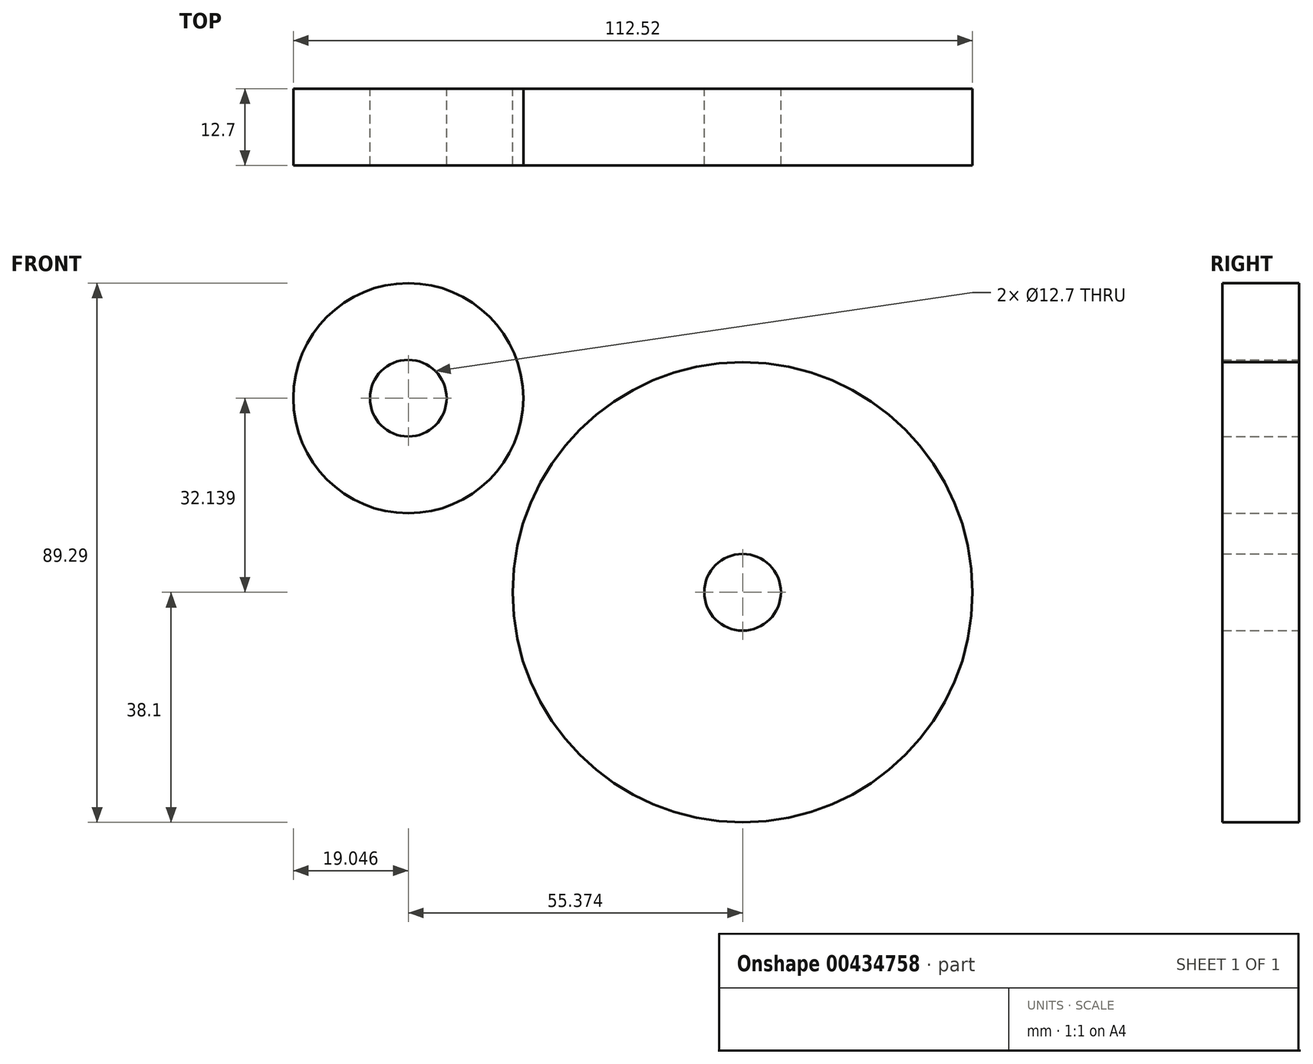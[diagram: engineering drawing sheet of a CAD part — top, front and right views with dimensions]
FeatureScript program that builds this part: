
annotation { "Feature Type Name" : "Feature", "Feature Type Description" : "" }
export const myFeature = defineFeature(function(context is Context, id is Id, definition is map)
    precondition{}
    {
        {
            var Q0;
            Q0=qCreatedBy(makeId("Front.planeOp"),FACE);
            var sketch = newSketch(context, id + "F0", { "sketchPlane" : qUnion([Q0])});
            skCircle(sketch, "E0", {"center": v(0, 0) * mm, "radius": 38.1 * mm});
            skCircle(sketch, "E1", {"center": v(0, 0) * mm, "radius": 6.35 * mm});
            skCircle(sketch, "E2", {"center": v(-55.37, 32.14) * mm, "radius": 19.05 * mm});
            skCircle(sketch, "E3", {"center": v(-55.37, 32.14) * mm, "radius": 6.35 * mm});
            skSolve(sketch);
        }
        {
            var Q0;
            Q0=makeQuery(id+"F0.imprint","IMPRINT",FACE,{"disambiguationData":[TD([[makeQuery(id+"F0.imprint","IMPRINT",EDGE,{"derivedFrom":sQuery(id+"F0.wireOp",EDGE,"E2")}),1.0]])]});
            var Q1;
            Q1=makeQuery(id+"F0.imprint","IMPRINT",FACE,{"disambiguationData":[TD([[makeQuery(id+"F0.imprint","IMPRINT",EDGE,{"derivedFrom":sQuery(id+"F0.wireOp",EDGE,"E0")}),1.0]])]});
            extrude(context, id + "F1", {"entities" : qUnion([Q0, Q1]), "depth" : 12.7 * mm});
        }
    });
